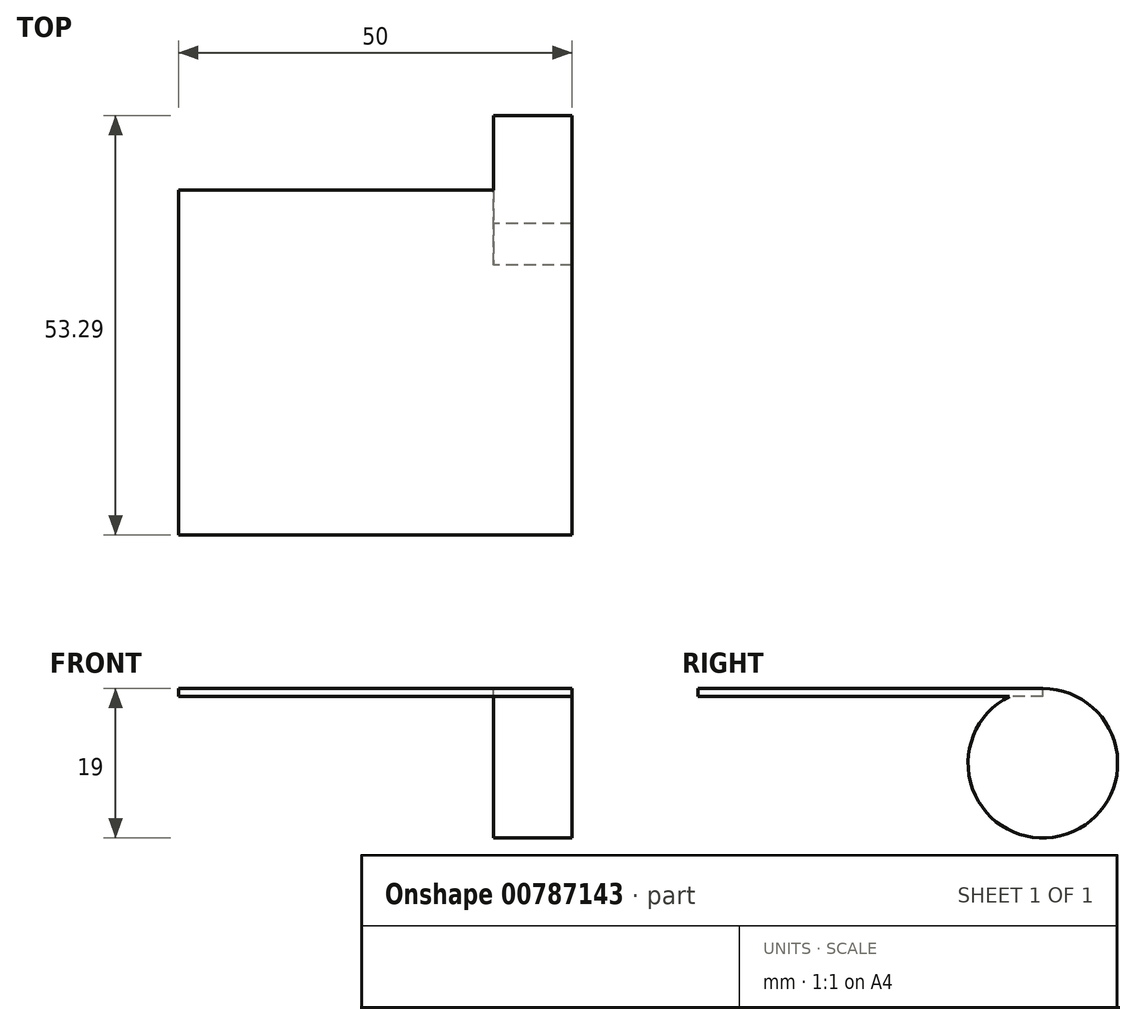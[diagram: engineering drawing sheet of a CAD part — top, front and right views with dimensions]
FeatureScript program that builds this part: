
annotation { "Feature Type Name" : "Feature", "Feature Type Description" : "" }
export const myFeature = defineFeature(function(context is Context, id is Id, definition is map)
    precondition{}
    {
        {
            var Q0;
            Q0=qCreatedBy(makeId("Right.planeOp"),FACE);
            var sketch = newSketch(context, id + "F0", { "sketchPlane" : qUnion([Q0])});
            skCircle(sketch, "E0", {"center": v(0, -8.5) * mm, "radius": 9.5 * mm});
            skLineSegment(sketch, "E1.bottom", {"start": v(0, 0) * mm, "end": v(-43.8, 0) * mm});
            skLineSegment(sketch, "E1.top", {"start": v(0, 1) * mm, "end": v(-43.8, 1) * mm});
            skLineSegment(sketch, "E1.left", {"start": v(0, 0) * mm, "end": v(0, 1) * mm});
            skLineSegment(sketch, "E1.right", {"start": v(-43.8, 0) * mm, "end": v(-43.8, 1) * mm});
            skLineSegment(sketch, "E2", {"start": v(0, -8.5) * mm, "end": v(0, 1) * mm, "construction": true});
            skSolve(sketch);
        }
        {
            var Q0;
            Q0 = qSketchRegion(id + "F0", true);
            extrude(context, id + "F1", {"entities" : qUnion([Q0]), "depth" : 10 * mm, "offsetDistance" : 25 * mm});
        }
        {
            var Q0;
            {var subQ0=sQuery(id+"F0.wireOp",EDGE,"E1.top");Q0=makeQuery(id+"F0.imprint","IMPRINT",FACE,{"disambiguationData":[TD([[makeQuery(id+"F0.imprint","IMPRINT",EDGE,{"derivedFrom":subQ0}),1.0]])]});}
            var Q1;
            {var subQ0=sQuery(id+"F0.wireOp",EDGE,"E1.left");Q1=makeQuery(id+"F0.imprint","IMPRINT",FACE,{"disambiguationData":[TD([[makeQuery(id+"F0.imprint","IMPRINT",EDGE,{"derivedFrom":subQ0}),1.0]])]});}
            extrude(context, id + "F2", {"entities" : qUnion([Q0, Q1]), "operationType" : NewBodyOperationType.ADD, "depth" : -40 * mm, "offsetDistance" : 25 * mm});
        }
    });
